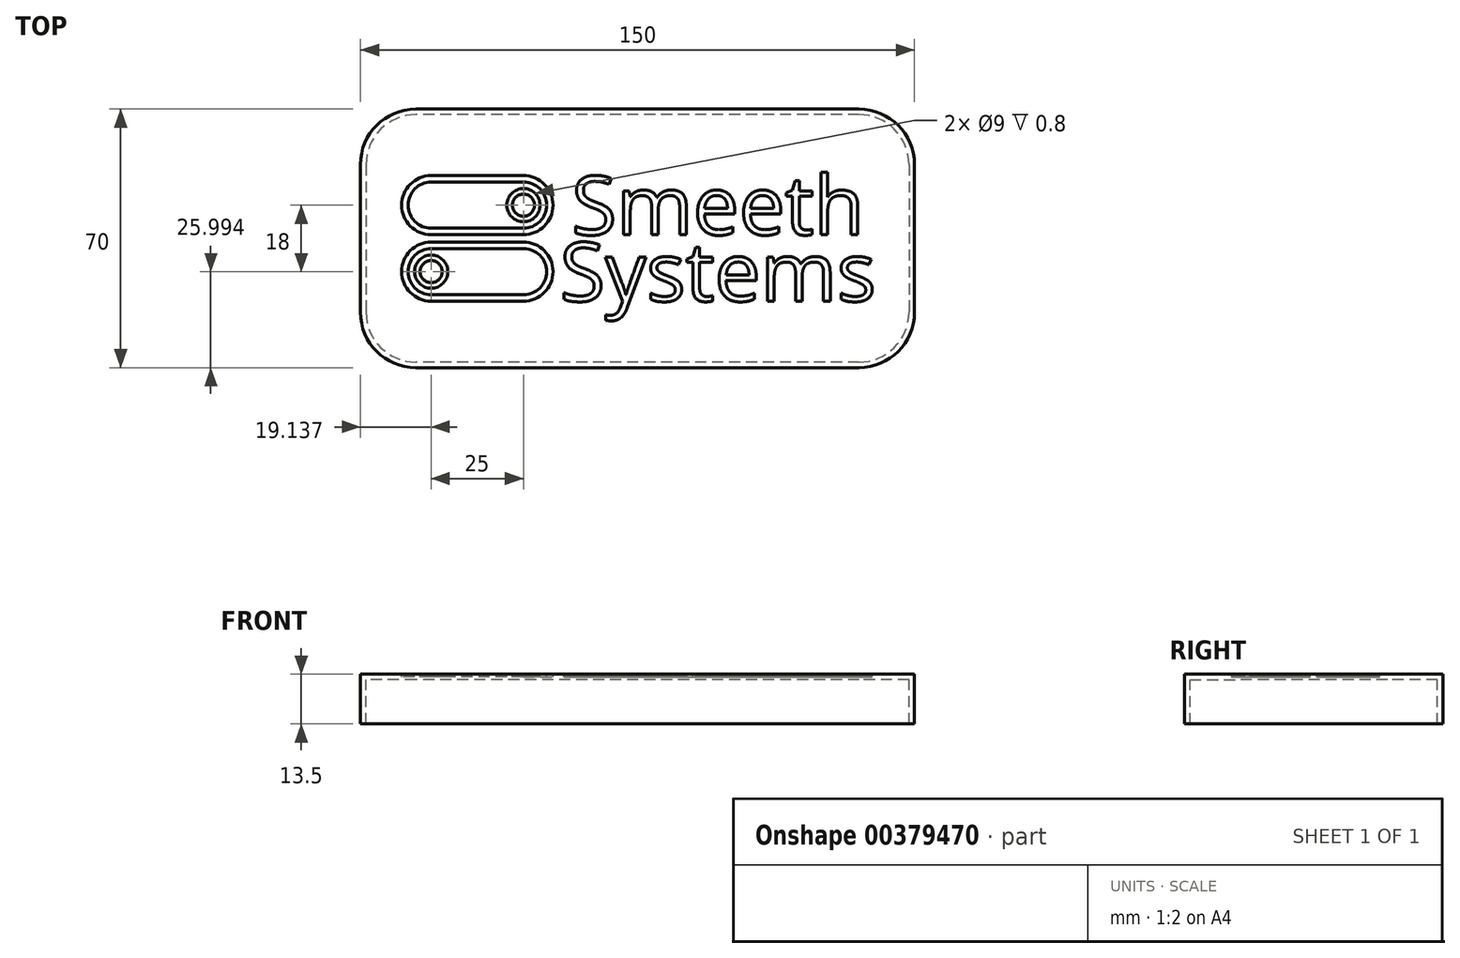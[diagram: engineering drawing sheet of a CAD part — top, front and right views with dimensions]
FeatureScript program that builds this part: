
annotation { "Feature Type Name" : "Feature", "Feature Type Description" : "" }
export const myFeature = defineFeature(function(context is Context, id is Id, definition is map)
    precondition{}
    {
        {
            var Q0;
            Q0=qCreatedBy(makeId("Top.planeOp"),FACE);
            var sketch = newSketch(context, id + "F0", { "sketchPlane" : qUnion([Q0])});
            skLineSegment(sketch, "E0.bottom", {"start": v(150, 15.22) * mm, "end": v(0, 15.22) * mm});
            skLineSegment(sketch, "E0.top", {"start": v(150, -54.78) * mm, "end": v(0, -54.78) * mm});
            skLineSegment(sketch, "E0.left", {"start": v(150, 15.22) * mm, "end": v(150, -54.78) * mm});
            skLineSegment(sketch, "E0.right", {"start": v(0, 15.22) * mm, "end": v(0, -54.78) * mm});
            skSolve(sketch);
        }
        {
            var Q0;
            Q0 = qSketchRegion(id + "F0", true);
            extrude(context, id + "F1", {"entities" : qUnion([Q0]), "oppositeDirection" : true, "depth" : 13.5 * mm, "offsetDistance" : 25 * mm});
        }
        {
            var Q0;
            Q0=qCreatedBy(makeId("Top.planeOp"),FACE);
            var sketch = newSketch(context, id + "F2", { "sketchPlane" : qUnion([Q0])});
            skText(sketch, "E1", { "text": "Smeeth", "fontName": "OpenSans-Regular.ttf"});
            skText(sketch, "E2", { "text": "Systems", "fontName": "OpenSans-Regular.ttf"});
            skLineSegment(sketch, "E3", {"start": v(44.14, -2.79) * mm, "end": v(19.14, -2.79) * mm});
            skLineSegment(sketch, "E4", {"start": v(44.14, -18.79) * mm, "end": v(19.14, -18.79) * mm});
            skLineSegment(sketch, "E5", {"start": v(44.14, -20.79) * mm, "end": v(19.14, -20.79) * mm});
            skLineSegment(sketch, "E6", {"start": v(19.14, -4.54) * mm, "end": v(44.14, -4.54) * mm});
            skLineSegment(sketch, "E7", {"start": v(44.14, -17.04) * mm, "end": v(19.14, -17.04) * mm});
            skLineSegment(sketch, "E8", {"start": v(19.14, -22.54) * mm, "end": v(44.14, -22.54) * mm});
            skLineSegment(sketch, "E9", {"start": v(44.14, -36.79) * mm, "end": v(19.14, -36.79) * mm});
            skLineSegment(sketch, "E10", {"start": v(19.14, -35.04) * mm, "end": v(44.14, -35.04) * mm});
            skArc(sketch, "E11", {"start": v(19.14, -2.79) * mm, "mid": v(11.14, -10.79) * mm, "end": v(19.14, -18.79) * mm});
            skArc(sketch, "E12", {"start": v(19.14, -4.54) * mm, "mid": v(12.89, -10.79) * mm, "end": v(19.14, -17.04) * mm});
            skArc(sketch, "E13", {"start": v(44.14, -4.54) * mm, "mid": v(50.39, -10.79) * mm, "end": v(44.14, -17.04) * mm});
            skArc(sketch, "E14", {"start": v(44.14, -2.79) * mm, "mid": v(52.14, -10.79) * mm, "end": v(44.14, -18.79) * mm});
            skArc(sketch, "E15", {"start": v(44.14, -20.79) * mm, "mid": v(52.14, -28.79) * mm, "end": v(44.14, -36.79) * mm});
            skArc(sketch, "E16", {"start": v(44.14, -22.54) * mm, "mid": v(50.39, -28.79) * mm, "end": v(44.14, -35.04) * mm});
            skArc(sketch, "E17", {"start": v(19.14, -20.79) * mm, "mid": v(11.14, -28.79) * mm, "end": v(19.14, -36.79) * mm});
            skArc(sketch, "E18", {"start": v(19.14, -22.54) * mm, "mid": v(12.89, -28.79) * mm, "end": v(19.14, -35.04) * mm});
            skCircle(sketch, "E19", {"center": v(19.14, -10.79) * mm, "radius": 4.5 * mm});
            skCircle(sketch, "E20", {"center": v(19.14, -10.79) * mm, "radius": 3 * mm});
            skCircle(sketch, "E21", {"center": v(44.14, -28.79) * mm, "radius": 4.5 * mm});
            skCircle(sketch, "E22", {"center": v(44.14, -28.79) * mm, "radius": 3 * mm});
            const initialGuessF2  = {"E1": [0.05714, -0.01879, 1, 0, 0.016], "E2": [0.054, -0.03679, 1, 0, 0.016]};
            skSetInitialGuess(sketch, initialGuessF2);
            skSolve(sketch);
        }
        {
            var Q0;
            Q0 = qSketchRegion(id + "F2", true);
            extrude(context, id + "F3", {"entities" : qUnion([Q0]), "operationType" : NewBodyOperationType.REMOVE, "oppositeDirection" : true, "depth" : 0.8 * mm, "offsetDistance" : 25 * mm});
        }
        {
            var Q0;
            Q0=makeQuery(id+"F3.boolean.opBoolean","SPLIT",FACE,{"disambiguationData":[TD([makeQuery(id+"F3.opExtrude","SWEPT_FACE",FACE,{"disambiguationData":[OSD([sQuery(id+"F2.wireOp",EDGE,"E6")])]})])],"derivedFrom":makeQuery(id+"F1.opExtrude","CAP_FACE",FACE,{"disambiguationData":[OSD([sQuery(id+"F0.wireOp",EDGE,"E0.bottom"),sQuery(id+"F0.wireOp",EDGE,"E0.top"),sQuery(id+"F0.wireOp",EDGE,"E0.left"),sQuery(id+"F0.wireOp",EDGE,"E0.right")])],"isStart":true})});
            var sketch = newSketch(context, id + "F4", { "sketchPlane" : qUnion([Q0])});
            skCircle(sketch, "E23", {"center": v(44.14, -10.79) * mm, "radius": 4.5 * mm});
            skCircle(sketch, "E24", {"center": v(44.14, -10.79) * mm, "radius": 3 * mm});
            skSolve(sketch);
        }
        {
            var Q0;
            Q0 = qSketchRegion(id + "F4", true);
            extrude(context, id + "F5", {"entities" : qUnion([Q0]), "operationType" : NewBodyOperationType.REMOVE, "oppositeDirection" : true, "depth" : 0.8 * mm, "offsetDistance" : 25 * mm});
        }
        {
            var Q0;
            Q0=makeQuery(id+"F3.boolean.opBoolean","SPLIT",FACE,{"disambiguationData":[TD([makeQuery(id+"F3.opExtrude","SWEPT_FACE",FACE,{"disambiguationData":[OSD([sQuery(id+"F2.wireOp",EDGE,"E8")])]})])],"derivedFrom":makeQuery(id+"F1.opExtrude","CAP_FACE",FACE,{"disambiguationData":[OSD([sQuery(id+"F0.wireOp",EDGE,"E0.bottom"),sQuery(id+"F0.wireOp",EDGE,"E0.top"),sQuery(id+"F0.wireOp",EDGE,"E0.left"),sQuery(id+"F0.wireOp",EDGE,"E0.right")])],"isStart":true})});
            var sketch = newSketch(context, id + "F6", { "sketchPlane" : qUnion([Q0])});
            skCircle(sketch, "E25", {"center": v(19.14, -28.79) * mm, "radius": 4.5 * mm});
            skCircle(sketch, "E26", {"center": v(19.14, -28.79) * mm, "radius": 3 * mm});
            skSolve(sketch);
        }
        {
            var Q0;
            Q0 = qSketchRegion(id + "F6", true);
            extrude(context, id + "F7", {"entities" : qUnion([Q0]), "operationType" : NewBodyOperationType.REMOVE, "oppositeDirection" : true, "depth" : 0.8 * mm, "offsetDistance" : 25 * mm});
        }
        {
            var Q0;
            Q0=makeQuery(id+"F1.opExtrude","SWEPT_EDGE",EDGE,{"disambiguationData":[OSD([sQuery(id+"F0.wireOp",EDGE,"E0.top"),sQuery(id+"F0.wireOp",EDGE,"E0.right")])]});
            var Q1;
            Q1=makeQuery(id+"F1.opExtrude","SWEPT_EDGE",EDGE,{"disambiguationData":[OSD([sQuery(id+"F0.wireOp",EDGE,"E0.top"),sQuery(id+"F0.wireOp",EDGE,"E0.left")])]});
            var Q2;
            Q2=makeQuery(id+"F1.opExtrude","SWEPT_EDGE",EDGE,{"disambiguationData":[OSD([sQuery(id+"F0.wireOp",EDGE,"E0.bottom"),sQuery(id+"F0.wireOp",EDGE,"E0.left")])]});
            var Q3;
            Q3=makeQuery(id+"F1.opExtrude","SWEPT_EDGE",EDGE,{"disambiguationData":[OSD([sQuery(id+"F0.wireOp",EDGE,"E0.bottom"),sQuery(id+"F0.wireOp",EDGE,"E0.right")])]});
            fillet(context, id + "F8", {"entities" : qUnion([Q0, Q1, Q2, Q3]), "radius" : 15 * mm, "tangentPropagation" : true, "allowEdgeOverflow" : false});
        }
        {
            var Q0;
            Q0=makeQuery(id+"F1.opExtrude","CAP_FACE",FACE,{"disambiguationData":[OSD([sQuery(id+"F0.wireOp",EDGE,"E0.bottom"),sQuery(id+"F0.wireOp",EDGE,"E0.top"),sQuery(id+"F0.wireOp",EDGE,"E0.left"),sQuery(id+"F0.wireOp",EDGE,"E0.right")])],"isStart":false});
            shell(context, id + "F9", {"entities" : qUnion([Q0]), "thickness" : 1.5 * mm});
        }
        {
            var Q0;
            Q0=makeQuery(id+"F9.opShell","OFFSET_FACE",FACE,{"disambiguationData":[OSD([sQuery(id+"F2.wireOp",EDGE,"E3"),sQuery(id+"F2.wireOp",EDGE,"E4"),sQuery(id+"F2.wireOp",EDGE,"E5"),sQuery(id+"F2.wireOp",EDGE,"E6"),sQuery(id+"F2.wireOp",EDGE,"E7"),sQuery(id+"F2.wireOp",EDGE,"E8"),sQuery(id+"F2.wireOp",EDGE,"E9"),sQuery(id+"F2.wireOp",EDGE,"E10"),sQuery(id+"F2.wireOp",EDGE,"E11"),sQuery(id+"F2.wireOp",EDGE,"E12"),sQuery(id+"F2.wireOp",EDGE,"E13"),sQuery(id+"F2.wireOp",EDGE,"E14"),sQuery(id+"F2.wireOp",EDGE,"E15"),sQuery(id+"F2.wireOp",EDGE,"E16"),sQuery(id+"F2.wireOp",EDGE,"E17"),sQuery(id+"F2.wireOp",EDGE,"E18"),sQuery(id+"F4.wireOp",EDGE,"E23"),sQuery(id+"F4.wireOp",EDGE,"E24"),sQuery(id+"F6.wireOp",EDGE,"E25"),sQuery(id+"F6.wireOp",EDGE,"E26")])]});
            var sketch = newSketch(context, id + "F10", { "sketchPlane" : qUnion([Q0])});
            skLineSegment(sketch, "E27.bottom", {"start": v(143.39, -4.88) * mm, "end": v(6.55, -4.88) * mm});
            skLineSegment(sketch, "E27.top", {"start": v(143.39, 46.28) * mm, "end": v(6.55, 46.28) * mm});
            skLineSegment(sketch, "E27.left", {"start": v(143.39, -4.88) * mm, "end": v(143.39, 46.28) * mm});
            skLineSegment(sketch, "E27.right", {"start": v(6.55, -4.88) * mm, "end": v(6.55, 46.28) * mm});
            skSolve(sketch);
        }
        {
            var Q0;
            Q0 = qSketchRegion(id + "F10", true);
            extrude(context, id + "F11", {"entities" : qUnion([Q0]), "operationType" : NewBodyOperationType.REMOVE, "oppositeDirection" : true, "depth" : 0.8 * mm, "offsetDistance" : 25 * mm});
        }
    });
